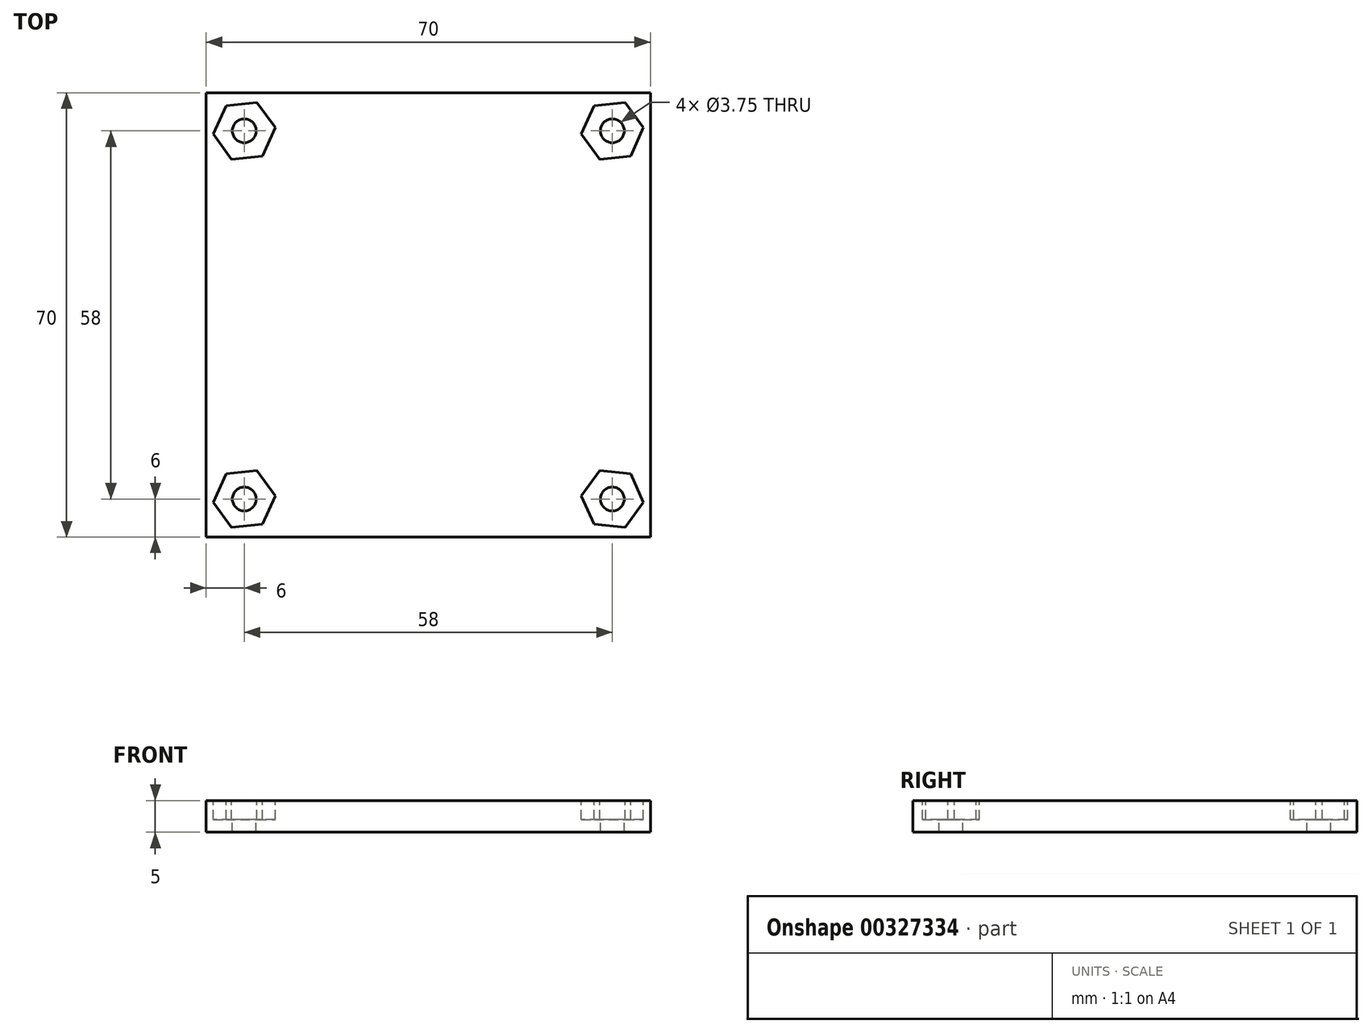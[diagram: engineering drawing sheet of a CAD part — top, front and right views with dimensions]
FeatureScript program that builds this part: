
annotation { "Feature Type Name" : "Feature", "Feature Type Description" : "" }
export const myFeature = defineFeature(function(context is Context, id is Id, definition is map)
    precondition{}
    {
        {
            var Q0;
            Q0=qCreatedBy(makeId("Top.planeOp"),FACE);
            var sketch = newSketch(context, id + "F0", { "sketchPlane" : qUnion([Q0])});
            skLineSegment(sketch, "E0.bottom", {"start": v(-35, -35) * mm, "end": v(35, -35) * mm});
            skLineSegment(sketch, "E0.top", {"start": v(-35, 35) * mm, "end": v(35, 35) * mm});
            skLineSegment(sketch, "E0.left", {"start": v(-35, -35) * mm, "end": v(-35, 35) * mm});
            skLineSegment(sketch, "E0.right", {"start": v(35, -35) * mm, "end": v(35, 35) * mm});
            skPoint(sketch, "E0.middle", {"position": v(0, 0) * mm});
            skSolve(sketch);
        }
        {
            var Q0;
            Q0 = qSketchRegion(id + "F0", true);
            extrude(context, id + "F1", {"entities" : qUnion([Q0]), "depth" : 5 * mm});
        }
        {
            var Q0;
            Q0=makeQuery(id+"F1.opExtrude","CAP_FACE",FACE,{"disambiguationData":[OSD([sQuery(id+"F0.wireOp",EDGE,"E0.bottom"),sQuery(id+"F0.wireOp",EDGE,"E0.top"),sQuery(id+"F0.wireOp",EDGE,"E0.left"),sQuery(id+"F0.wireOp",EDGE,"E0.right")])],"isStart":false});
            var sketch = newSketch(context, id + "F2", { "sketchPlane" : qUnion([Q0])});
            skLineSegment(sketch, "E1.bottom", {"start": v(-29, -29) * mm, "end": v(29, -29) * mm});
            skLineSegment(sketch, "E1.top", {"start": v(-29, 29) * mm, "end": v(29, 29) * mm});
            skLineSegment(sketch, "E1.left", {"start": v(-29, -29) * mm, "end": v(-29, 29) * mm});
            skLineSegment(sketch, "E1.right", {"start": v(29, -29) * mm, "end": v(29, 29) * mm});
            skPoint(sketch, "E1.middle", {"position": v(0, 0) * mm});
            skCircle(sketch, "E2.cCircle", {"center": v(-29, 29) * mm, "radius": 4.25 * mm, "construction": true});
            skLineSegment(sketch, "E2.0", {"start": v(-31, 24.52) * mm, "end": v(-33.88, 28.5) * mm});
            skLineSegment(sketch, "E2.1", {"start": v(-33.88, 28.5) * mm, "end": v(-31.88, 32.97) * mm});
            skLineSegment(sketch, "E2.2", {"start": v(-31.88, 32.97) * mm, "end": v(-27, 33.48) * mm});
            skLineSegment(sketch, "E2.3", {"start": v(-27, 33.48) * mm, "end": v(-24.12, 29.5) * mm});
            skLineSegment(sketch, "E2.4", {"start": v(-24.12, 29.5) * mm, "end": v(-26.12, 25.03) * mm});
            skLineSegment(sketch, "E2.5", {"start": v(-26.12, 25.03) * mm, "end": v(-31, 24.52) * mm});
            skPoint(sketch, "E2.0.midPoint", {"position": v(-32.44, 26.5) * mm});
            skCircle(sketch, "E3.cCircle", {"center": v(29, 29) * mm, "radius": 4.25 * mm, "construction": true});
            skLineSegment(sketch, "E3.0", {"start": v(27, 24.52) * mm, "end": v(24.12, 28.5) * mm});
            skLineSegment(sketch, "E3.1", {"start": v(24.12, 28.5) * mm, "end": v(26.12, 32.97) * mm});
            skLineSegment(sketch, "E3.2", {"start": v(26.12, 32.97) * mm, "end": v(31, 33.48) * mm});
            skLineSegment(sketch, "E3.3", {"start": v(31, 33.48) * mm, "end": v(33.88, 29.5) * mm});
            skLineSegment(sketch, "E3.4", {"start": v(33.88, 29.5) * mm, "end": v(31.88, 25.03) * mm});
            skLineSegment(sketch, "E3.5", {"start": v(31.88, 25.03) * mm, "end": v(27, 24.52) * mm});
            skPoint(sketch, "E3.0.midPoint", {"position": v(25.56, 26.5) * mm});
            skCircle(sketch, "E4.cCircle", {"center": v(29, -29) * mm, "radius": 4.25 * mm, "construction": true});
            skLineSegment(sketch, "E4.0", {"start": v(24.12, -28.5) * mm, "end": v(27, -24.52) * mm});
            skLineSegment(sketch, "E4.1", {"start": v(27, -24.52) * mm, "end": v(31.88, -25.03) * mm});
            skLineSegment(sketch, "E4.2", {"start": v(31.88, -25.03) * mm, "end": v(33.88, -29.5) * mm});
            skLineSegment(sketch, "E4.3", {"start": v(33.88, -29.5) * mm, "end": v(31, -33.48) * mm});
            skLineSegment(sketch, "E4.4", {"start": v(31, -33.48) * mm, "end": v(26.12, -32.97) * mm});
            skLineSegment(sketch, "E4.5", {"start": v(26.12, -32.97) * mm, "end": v(24.12, -28.5) * mm});
            skPoint(sketch, "E4.0.midPoint", {"position": v(25.56, -26.5) * mm});
            skCircle(sketch, "E5.cCircle", {"center": v(-29, -29) * mm, "radius": 4.25 * mm, "construction": true});
            skLineSegment(sketch, "E5.0", {"start": v(-27, -24.52) * mm, "end": v(-24.12, -28.5) * mm});
            skLineSegment(sketch, "E5.1", {"start": v(-24.12, -28.5) * mm, "end": v(-26.12, -32.97) * mm});
            skLineSegment(sketch, "E5.2", {"start": v(-26.12, -32.97) * mm, "end": v(-31, -33.48) * mm});
            skLineSegment(sketch, "E5.3", {"start": v(-31, -33.48) * mm, "end": v(-33.88, -29.5) * mm});
            skLineSegment(sketch, "E5.4", {"start": v(-33.88, -29.5) * mm, "end": v(-31.88, -25.03) * mm});
            skLineSegment(sketch, "E5.5", {"start": v(-31.88, -25.03) * mm, "end": v(-27, -24.52) * mm});
            skPoint(sketch, "E5.0.midPoint", {"position": v(-25.56, -26.5) * mm});
            skSolve(sketch);
        }
        {
            var Q0;
            {var subQ1=sQuery(id+"F2.wireOp",EDGE,"E5.0");Q0=makeQuery(id+"F2.imprint","IMPRINT",FACE,{"disambiguationData":[TD([[makeQuery(id+"F2.imprint","IMPRINT",EDGE,{"derivedFrom":subQ1}),-1.0]])]});}
            var Q1;
            {var subQ0=sQuery(id+"F2.wireOp",EDGE,"E5.2");Q1=makeQuery(id+"F2.imprint","IMPRINT",FACE,{"disambiguationData":[TD([[makeQuery(id+"F2.imprint","IMPRINT",EDGE,{"derivedFrom":subQ0}),-1.0]])]});}
            var Q2;
            {var subQ0=sQuery(id+"F2.wireOp",EDGE,"E4.0");Q2=makeQuery(id+"F2.imprint","IMPRINT",FACE,{"disambiguationData":[TD([[makeQuery(id+"F2.imprint","IMPRINT",EDGE,{"derivedFrom":subQ0}),-1.0]])]});}
            var Q3;
            {var subQ0=sQuery(id+"F2.wireOp",EDGE,"E4.2");Q3=makeQuery(id+"F2.imprint","IMPRINT",FACE,{"disambiguationData":[TD([[makeQuery(id+"F2.imprint","IMPRINT",EDGE,{"derivedFrom":subQ0}),-1.0]])]});}
            var Q4;
            {var subQ0=sQuery(id+"F2.wireOp",EDGE,"E2.0");Q4=makeQuery(id+"F2.imprint","IMPRINT",FACE,{"disambiguationData":[TD([[makeQuery(id+"F2.imprint","IMPRINT",EDGE,{"derivedFrom":subQ0}),-1.0]])]});}
            var Q5;
            {var subQ0=sQuery(id+"F2.wireOp",EDGE,"E1.left");var subQ1=sQuery(id+"F2.wireOp",EDGE,"E1.top");var subQ2=makeQuery(id+"F2.imprint","INTERSECT",VERTEX,{"derivedFrom":[subQ1,subQ0]});Q5=makeQuery(id+"F2.imprint","IMPRINT",FACE,{"disambiguationData":[TD([[makeQuery(id+"F2.imprint","IMPRINT",EDGE,{"disambiguationData":[TD([[subQ2,-1.0]])],"derivedFrom":subQ1}),-1.0]])]});}
            var Q6;
            {var subQ1=sQuery(id+"F2.wireOp",EDGE,"E3.0");Q6=makeQuery(id+"F2.imprint","IMPRINT",FACE,{"disambiguationData":[TD([[makeQuery(id+"F2.imprint","IMPRINT",EDGE,{"derivedFrom":subQ1}),-1.0]])]});}
            var Q7;
            {var subQ0=sQuery(id+"F2.wireOp",EDGE,"E3.2");Q7=makeQuery(id+"F2.imprint","IMPRINT",FACE,{"disambiguationData":[TD([[makeQuery(id+"F2.imprint","IMPRINT",EDGE,{"derivedFrom":subQ0}),-1.0]])]});}
            extrude(context, id + "F3", {"entities" : qUnion([Q0, Q1, Q2, Q3, Q4, Q5, Q6, Q7]), "operationType" : NewBodyOperationType.REMOVE, "oppositeDirection" : true, "depth" : 3 * mm});
        }
        {
            var Q0;
            Q0=makeQuery(id+"F1.opExtrude","CAP_FACE",FACE,{"disambiguationData":[OSD([sQuery(id+"F0.wireOp",EDGE,"E0.bottom"),sQuery(id+"F0.wireOp",EDGE,"E0.top"),sQuery(id+"F0.wireOp",EDGE,"E0.left"),sQuery(id+"F0.wireOp",EDGE,"E0.right")])],"isStart":false});
            var sketch = newSketch(context, id + "F4", { "sketchPlane" : qUnion([Q0])});
            skLineSegment(sketch, "E6.bottom", {"start": v(-29, -29) * mm, "end": v(29, -29) * mm});
            skLineSegment(sketch, "E6.top", {"start": v(-29, 29) * mm, "end": v(29, 29) * mm});
            skLineSegment(sketch, "E6.left", {"start": v(-29, -29) * mm, "end": v(-29, 29) * mm});
            skLineSegment(sketch, "E6.right", {"start": v(29, -29) * mm, "end": v(29, 29) * mm});
            skPoint(sketch, "E6.middle", {"position": v(0, 0) * mm});
            skCircle(sketch, "E7", {"center": v(-29, 29) * mm, "radius": 1.88 * mm});
            skCircle(sketch, "E8", {"center": v(29, 29) * mm, "radius": 1.88 * mm});
            skCircle(sketch, "E9", {"center": v(-29, -29) * mm, "radius": 1.88 * mm});
            skCircle(sketch, "E10", {"center": v(29, -29) * mm, "radius": 1.88 * mm});
            skSolve(sketch);
        }
        {
            var Q0;
            {var subQ0=sQuery(id+"F4.wireOp",EDGE,"E6.left");var subQ1=sQuery(id+"F4.wireOp",EDGE,"E6.bottom");var subQ2=makeQuery(id+"F4.imprint","INTERSECT",VERTEX,{"derivedFrom":[subQ1,subQ0]});Q0=makeQuery(id+"F4.imprint","IMPRINT",FACE,{"disambiguationData":[TD([[makeQuery(id+"F4.imprint","IMPRINT",EDGE,{"disambiguationData":[TD([[subQ2,-1.0]])],"derivedFrom":subQ1}),1.0]])]});}
            var Q1;
            {var subQ0=sQuery(id+"F4.wireOp",EDGE,"E6.left");var subQ1=sQuery(id+"F4.wireOp",EDGE,"E6.bottom");var subQ2=makeQuery(id+"F4.imprint","INTERSECT",VERTEX,{"derivedFrom":[subQ1,subQ0]});Q1=makeQuery(id+"F4.imprint","IMPRINT",FACE,{"disambiguationData":[TD([[makeQuery(id+"F4.imprint","IMPRINT",EDGE,{"disambiguationData":[TD([[subQ2,-1.0]])],"derivedFrom":subQ1}),-1.0]])]});}
            var Q2;
            {var subQ0=sQuery(id+"F4.wireOp",EDGE,"E6.right");var subQ1=sQuery(id+"F4.wireOp",EDGE,"E6.bottom");var subQ2=makeQuery(id+"F4.imprint","INTERSECT",VERTEX,{"derivedFrom":[subQ1,subQ0]});Q2=makeQuery(id+"F4.imprint","IMPRINT",FACE,{"disambiguationData":[TD([[makeQuery(id+"F4.imprint","IMPRINT",EDGE,{"disambiguationData":[TD([[subQ2,1.0]])],"derivedFrom":subQ1}),1.0]])]});}
            var Q3;
            {var subQ0=sQuery(id+"F4.wireOp",EDGE,"E6.right");var subQ1=sQuery(id+"F4.wireOp",EDGE,"E6.bottom");var subQ2=makeQuery(id+"F4.imprint","INTERSECT",VERTEX,{"derivedFrom":[subQ1,subQ0]});Q3=makeQuery(id+"F4.imprint","IMPRINT",FACE,{"disambiguationData":[TD([[makeQuery(id+"F4.imprint","IMPRINT",EDGE,{"disambiguationData":[TD([[subQ2,1.0]])],"derivedFrom":subQ1}),-1.0]])]});}
            var Q4;
            {var subQ0=sQuery(id+"F4.wireOp",EDGE,"E6.left");var subQ1=sQuery(id+"F4.wireOp",EDGE,"E6.top");var subQ2=makeQuery(id+"F4.imprint","INTERSECT",VERTEX,{"derivedFrom":[subQ1,subQ0]});Q4=makeQuery(id+"F4.imprint","IMPRINT",FACE,{"disambiguationData":[TD([[makeQuery(id+"F4.imprint","IMPRINT",EDGE,{"disambiguationData":[TD([[subQ2,-1.0]])],"derivedFrom":subQ1}),1.0]])]});}
            var Q5;
            {var subQ0=sQuery(id+"F4.wireOp",EDGE,"E6.left");var subQ1=sQuery(id+"F4.wireOp",EDGE,"E6.top");var subQ2=makeQuery(id+"F4.imprint","INTERSECT",VERTEX,{"derivedFrom":[subQ1,subQ0]});Q5=makeQuery(id+"F4.imprint","IMPRINT",FACE,{"disambiguationData":[TD([[makeQuery(id+"F4.imprint","IMPRINT",EDGE,{"disambiguationData":[TD([[subQ2,-1.0]])],"derivedFrom":subQ1}),-1.0]])]});}
            var Q6;
            {var subQ0=sQuery(id+"F4.wireOp",EDGE,"E6.right");var subQ1=sQuery(id+"F4.wireOp",EDGE,"E6.top");var subQ2=makeQuery(id+"F4.imprint","INTERSECT",VERTEX,{"derivedFrom":[subQ1,subQ0]});Q6=makeQuery(id+"F4.imprint","IMPRINT",FACE,{"disambiguationData":[TD([[makeQuery(id+"F4.imprint","IMPRINT",EDGE,{"disambiguationData":[TD([[subQ2,1.0]])],"derivedFrom":subQ1}),-1.0]])]});}
            var Q7;
            {var subQ0=sQuery(id+"F4.wireOp",EDGE,"E6.right");var subQ1=sQuery(id+"F4.wireOp",EDGE,"E6.top");var subQ2=makeQuery(id+"F4.imprint","INTERSECT",VERTEX,{"derivedFrom":[subQ1,subQ0]});Q7=makeQuery(id+"F4.imprint","IMPRINT",FACE,{"disambiguationData":[TD([[makeQuery(id+"F4.imprint","IMPRINT",EDGE,{"disambiguationData":[TD([[subQ2,1.0]])],"derivedFrom":subQ1}),1.0]])]});}
            extrude(context, id + "F5", {"entities" : qUnion([Q0, Q1, Q2, Q3, Q4, Q5, Q6, Q7]), "operationType" : NewBodyOperationType.REMOVE, "oppositeDirection" : true, "depth" : 25 * mm});
        }
    });
